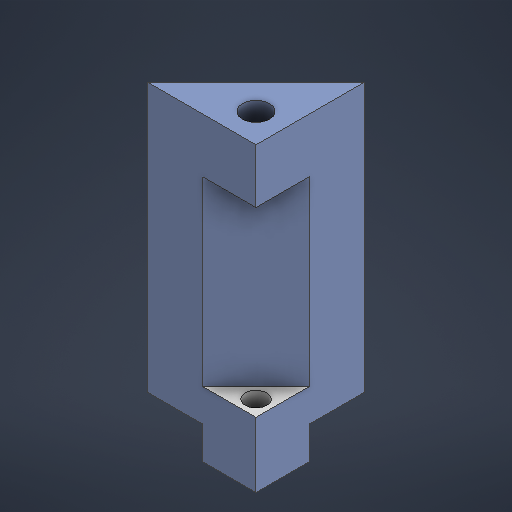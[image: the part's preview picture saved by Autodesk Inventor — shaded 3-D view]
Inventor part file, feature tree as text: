
AUTODESK INVENTOR PART (.ipt)
format: ipt  version: 2025.1 (Build 291241000, 241)  size: 533,504 bytes
history: native  units: in
note: dims shown in document units (in); Inventor stores cm internally (conversion verified against a paired STEP export)
features: projected_geometry x16, sketch x10, extrude x9, other x1
ambient origin geometry x8: Origin, YZ Plane, XZ Plane, XY Plane, X Axis, Y Axis, Z Axis, Center Point
bodies: Solid1 (feature_tree)
feature tree (36):
  extrude  "Extrusion1"  Depth=0.1949in
  extrude  "Extrusion2"  Depth=0.3937in
  extrude  "Extrusion3"  Depth=0.3937in TaperAngle=0.0deg
  extrude  "Extrusion4"  Depth=0.1969in TaperAngle=0.0deg
  extrude  "Extrusion5"  Depth=0.1969in TaperAngle=0.0deg
  extrude  "Extrusion6"  Depth=0.1299in
  extrude  "Extrusion7"  Depth=0.105in
  sketch  "Sketch9"  dims[d20=0.0571in d21=0.0571in]
  extrude  "Extrusion8"  Depth=0.0571in
  extrude  "Extrusion9"  Depth=0.3937in TaperAngle=0.0deg
  sketch  "Sketch1"  dims[d0=0.1949in d1=0.1949in]
  sketch  "Sketch2"  dims[d2=0.2362in d3=0.0in d4=0.3937in]
  sketch  "Sketch3"  dims[d5=0.3937in d6=0.0787in d7=0.0in]
  sketch  "Sketch4"  dims[d8=0.7776in d9=0.0in d10=0.1969in d11=0.0in]
  sketch  "Sketch6"  dims[d12=0.0984in d13=0.1969in d14=0.0in]
  sketch  "Sketch7"  dims[d15=0.0787in d16=0.0in d17=0.1299in]
  sketch  "Sketch8"  dims[d18=0.105in d19=0.105in]
  sketch  "Sketch10"  dims[d22=0.0787in d23=0.3937in d24=0.0in]
  projected_geometry  "Projected Loop1"
  sketch  "Sketch11"  dims[d25=45.0deg d26=0.6496in d27=135.0deg d28=0.1969in d29=0.0984in d30=0.1575in d31=0.0in d32=0.1181in d33=0.0in d34=0.0197in d35=0.0344in]
  projected_geometry  "Projected Loop2"
  projected_geometry  "Projected Loop3"
  projected_geometry  "Projected Loop4"
  projected_geometry  "Projected Loop5"
  projected_geometry  "Projected Loop6"
  projected_geometry  "Projected Loop7"
  projected_geometry  "Projected Loop8"
  projected_geometry  "Projected Loop9"
  projected_geometry  "Projected Loop10"
  projected_geometry  "Projected Loop11"
  projected_geometry  "Projected Loop12"
  projected_geometry  "Projected Loop13"
  projected_geometry  "Projected Loop14"
  projected_geometry  "Projected Loop15"
  projected_geometry  "Projected Loop16"
  other  "Finish1"
